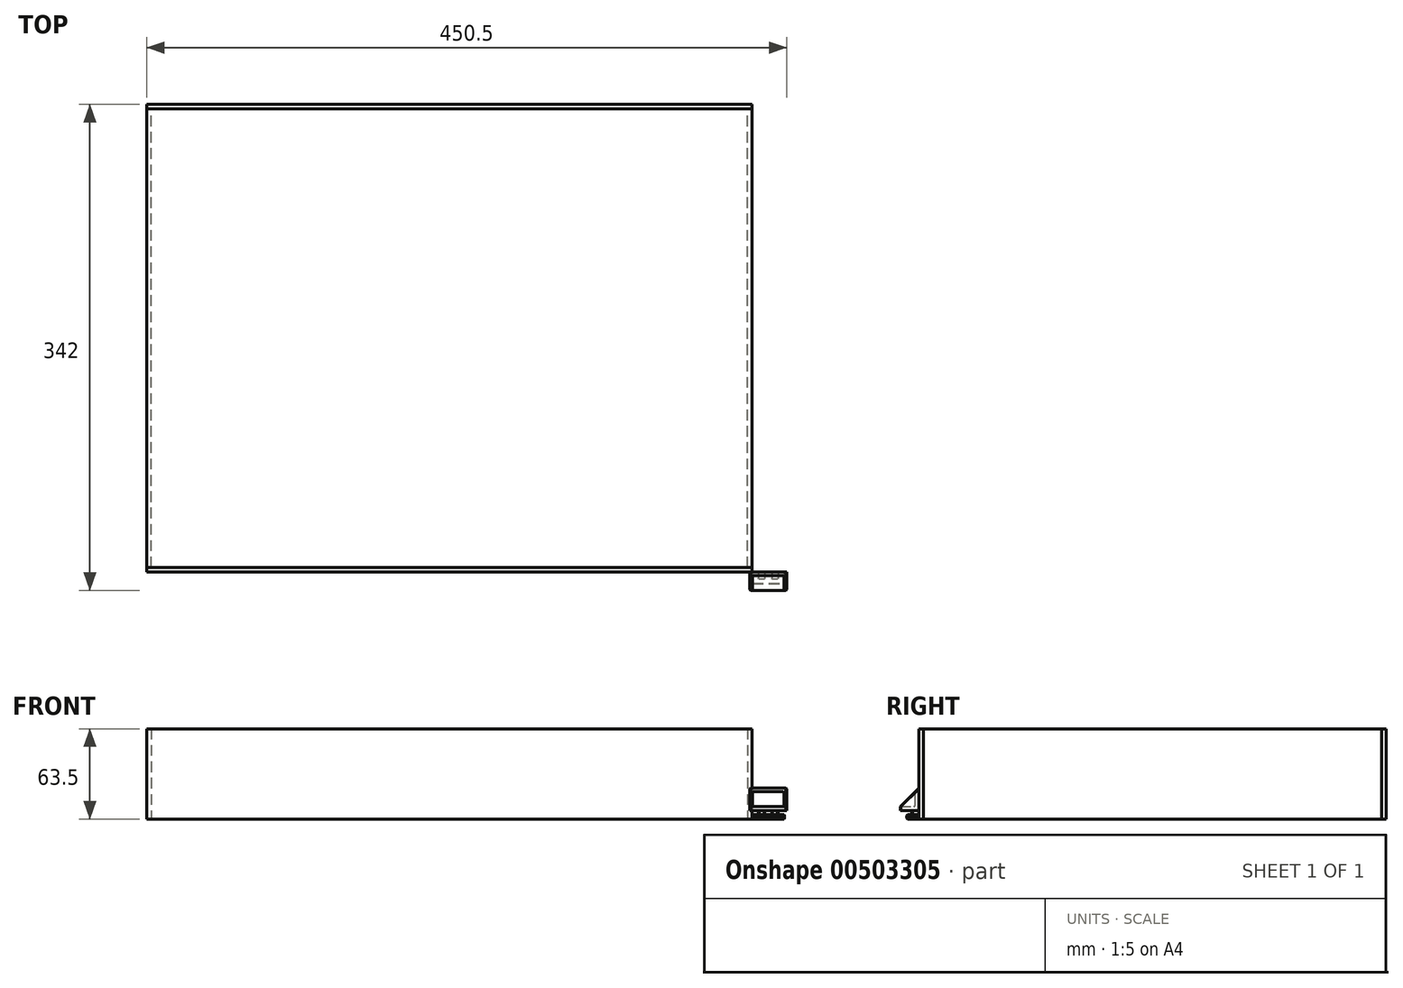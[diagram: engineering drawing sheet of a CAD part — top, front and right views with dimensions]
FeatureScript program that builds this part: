
annotation { "Feature Type Name" : "Feature", "Feature Type Description" : "" }
export const myFeature = defineFeature(function(context is Context, id is Id, definition is map)
    precondition{}
    {
        {
            var Q0;
            Q0=qCreatedBy(makeId("Top.planeOp"),FACE);
            var sketch = newSketch(context, id + "F0", { "sketchPlane" : qUnion([Q0])});
            skLineSegment(sketch, "E0.bottom", {"start": v(0, 0) * mm, "end": v(23, 0) * mm});
            skLineSegment(sketch, "E0.top", {"start": v(0, 8.5) * mm, "end": v(23, 8.5) * mm});
            skLineSegment(sketch, "E0.left", {"start": v(0, 0) * mm, "end": v(0, 8.5) * mm});
            skLineSegment(sketch, "E0.right", {"start": v(23, 0) * mm, "end": v(23, 8.5) * mm});
            skSolve(sketch);
        }
        {
            var Q0;
            Q0=makeQuery(id+"F0.imprint","IMPRINT",FACE,{"disambiguationData":[TD([[makeQuery(id+"F0.imprint","IMPRINT",EDGE,{"derivedFrom":sQuery(id+"F0.wireOp",EDGE,"E0.bottom")}),1.0]])]});
            extrude(context, id + "F1", {"entities" : qUnion([Q0]), "depth" : 3 * mm});
        }
        {
            var Q0;
            Q0=makeQuery(id+"F1.opExtrude","CAP_FACE",FACE,{"disambiguationData":[OSD([sQuery(id+"F0.wireOp",EDGE,"E0.bottom"),sQuery(id+"F0.wireOp",EDGE,"E0.top"),sQuery(id+"F0.wireOp",EDGE,"E0.left"),sQuery(id+"F0.wireOp",EDGE,"E0.right")])],"isStart":false});
            var sketch = newSketch(context, id + "F2", { "sketchPlane" : qUnion([Q0])});
            skLineSegment(sketch, "E1", {"start": v(11.5, 8.5) * mm, "end": v(11.5, 0) * mm, "construction": true});
            skLineSegment(sketch, "E2.bottom", {"start": v(4.57, 8.5) * mm, "end": v(9.07, 8.5) * mm});
            skLineSegment(sketch, "E2.top", {"start": v(4.57, 3.5) * mm, "end": v(9.07, 3.5) * mm});
            skLineSegment(sketch, "E2.left", {"start": v(4.57, 8.5) * mm, "end": v(4.57, 3.5) * mm});
            skLineSegment(sketch, "E2.right", {"start": v(9.07, 8.5) * mm, "end": v(9.07, 3.5) * mm});
            skLineSegment(sketch, "E3.bottom", {"start": v(13.92, 8.5) * mm, "end": v(18.42, 8.5) * mm});
            skLineSegment(sketch, "E3.top", {"start": v(13.92, 3.5) * mm, "end": v(18.42, 3.5) * mm});
            skLineSegment(sketch, "E3.left", {"start": v(13.92, 8.5) * mm, "end": v(13.92, 3.5) * mm});
            skLineSegment(sketch, "E3.right", {"start": v(18.42, 8.5) * mm, "end": v(18.42, 3.5) * mm});
            skSolve(sketch);
        }
        {
            var Q0;
            Q0 = qSketchRegion(id + "F2", true);
            extrude(context, id + "F3", {"entities" : qUnion([Q0]), "operationType" : NewBodyOperationType.ADD, "depth" : 2.85 * mm});
        }
        {
            var Q0;
            Q0=makeQuery(id+"F3.opExtrude","CAP_FACE",FACE,{"disambiguationData":[OSD([sQuery(id+"F2.wireOp",EDGE,"E3.bottom"),sQuery(id+"F2.wireOp",EDGE,"E3.top"),sQuery(id+"F2.wireOp",EDGE,"E3.left"),sQuery(id+"F2.wireOp",EDGE,"E3.right")])],"isStart":false});
            var sketch = newSketch(context, id + "F4", { "sketchPlane" : qUnion([Q0])});
            skLineSegment(sketch, "E4.bottom", {"start": v(24.5, 8.5) * mm, "end": v(-1.5, 8.5) * mm});
            skLineSegment(sketch, "E4.top", {"start": v(24.5, -4.5) * mm, "end": v(-1.5, -4.5) * mm});
            skLineSegment(sketch, "E4.left", {"start": v(24.5, 8.5) * mm, "end": v(24.5, -4.5) * mm});
            skLineSegment(sketch, "E4.right", {"start": v(-1.5, 8.5) * mm, "end": v(-1.5, -4.5) * mm});
            skLineSegment(sketch, "E5", {"start": v(11.5, -4.5) * mm, "end": v(11.5, 8.5) * mm, "construction": true});
            skSolve(sketch);
        }
        {
            var Q0;
            Q0 = qSketchRegion(id + "F4", true);
            extrude(context, id + "F5", {"entities" : qUnion([Q0]), "operationType" : NewBodyOperationType.ADD, "depth" : 3 * mm});
        }
        {
            var Q0;
            Q0=makeQuery(id+"F5.opExtrude","SWEPT_FACE",FACE,{"disambiguationData":[OSD([sQuery(id+"F4.wireOp",EDGE,"E4.left")])]});
            var sketch = newSketch(context, id + "F6", { "sketchPlane" : qUnion([Q0])});
            skLineSegment(sketch, "E6.0", {"start": v(8.5, 8.85) * mm, "end": v(-4.5, 8.85) * mm});
            skLineSegment(sketch, "E7", {"start": v(8.5, 8.85) * mm, "end": v(8.5, 21.85) * mm});
            skLineSegment(sketch, "E8", {"start": v(8.5, 21.85) * mm, "end": v(-4.5, 8.85) * mm});
            skSolve(sketch);
        }
        {
            var Q0;
            Q0=makeQuery(id+"F6.imprint","IMPRINT",FACE,{"disambiguationData":[TD([[makeQuery(id+"F6.imprint","IMPRINT",EDGE,{"derivedFrom":sQuery(id+"F6.wireOp",EDGE,"E6.0")}),-1.0]])]});
            var Q1;
            Q1=makeQuery(id+"F5.opExtrude","SWEPT_FACE",FACE,{"disambiguationData":[OSD([sQuery(id+"F4.wireOp",EDGE,"E4.right")])]});
            extrude(context, id + "F7", {"entities" : qUnion([Q0]), "operationType" : NewBodyOperationType.ADD, "endBound" : BoundingType.UP_TO_SURFACE, "oppositeDirection" : true, "endBoundEntityFace" : qUnion([Q1]), "depth" : 25 * mm});
        }
        {
            var Q0;
            Q0=makeQuery(id+"F3.opExtrude","SWEPT_EDGE",EDGE,{"disambiguationData":[OSD([sQuery(id+"F2.wireOp",EDGE,"E2.top"),sQuery(id+"F2.wireOp",EDGE,"E2.left")])]});
            var Q1;
            Q1=makeQuery(id+"F3.opExtrude","SWEPT_EDGE",EDGE,{"disambiguationData":[OSD([sQuery(id+"F2.wireOp",EDGE,"E2.top"),sQuery(id+"F2.wireOp",EDGE,"E2.right")])]});
            var Q2;
            Q2=makeQuery(id+"F3.opExtrude","SWEPT_EDGE",EDGE,{"disambiguationData":[OSD([sQuery(id+"F2.wireOp",EDGE,"E3.top"),sQuery(id+"F2.wireOp",EDGE,"E3.left")])]});
            var Q3;
            Q3=makeQuery(id+"F3.opExtrude","SWEPT_EDGE",EDGE,{"disambiguationData":[OSD([sQuery(id+"F2.wireOp",EDGE,"E3.top"),sQuery(id+"F2.wireOp",EDGE,"E3.right")])]});
            chamfer(context, id + "F8", {"entities" : qUnion([Q0, Q1, Q2, Q3]), "width" : .5 * mm, "tangentPropagation" : true});
        }
        {
            var Q0;
            Q0=makeQuery(id+"F3.opExtrude","CAP_EDGE",EDGE,{"disambiguationData":[OSD([sQuery(id+"F2.wireOp",EDGE,"E2.left")])],"isStart":false});
            var Q1;
            Q1=makeQuery(id+"F8.opChamfer","BLEND_EDGE",EDGE,{"blendedFrom":[makeQuery(id+"F3.opExtrude","SWEPT_EDGE",EDGE,{"disambiguationData":[OSD([sQuery(id+"F2.wireOp",EDGE,"E2.top"),sQuery(id+"F2.wireOp",EDGE,"E2.left")])]}),makeQuery(id+"F5.opExtrude","CAP_FACE",FACE,{"disambiguationData":[OSD([sQuery(id+"F4.wireOp",EDGE,"E4.bottom"),sQuery(id+"F4.wireOp",EDGE,"E4.top"),sQuery(id+"F4.wireOp",EDGE,"E4.left"),sQuery(id+"F4.wireOp",EDGE,"E4.right")])],"isStart":true})],"blendedInto":[makeQuery(id+"F5.opExtrude","CAP_FACE",FACE,{"disambiguationData":[OSD([sQuery(id+"F4.wireOp",EDGE,"E4.bottom"),sQuery(id+"F4.wireOp",EDGE,"E4.top"),sQuery(id+"F4.wireOp",EDGE,"E4.left"),sQuery(id+"F4.wireOp",EDGE,"E4.right")])],"isStart":true})]});
            var Q2;
            Q2=makeQuery(id+"F3.opExtrude","CAP_EDGE",EDGE,{"disambiguationData":[OSD([sQuery(id+"F2.wireOp",EDGE,"E2.top")])],"isStart":false});
            var Q3;
            Q3=makeQuery(id+"F8.opChamfer","BLEND_EDGE",EDGE,{"blendedFrom":[makeQuery(id+"F3.opExtrude","SWEPT_EDGE",EDGE,{"disambiguationData":[OSD([sQuery(id+"F2.wireOp",EDGE,"E2.top"),sQuery(id+"F2.wireOp",EDGE,"E2.right")])]}),makeQuery(id+"F5.opExtrude","CAP_FACE",FACE,{"disambiguationData":[OSD([sQuery(id+"F4.wireOp",EDGE,"E4.bottom"),sQuery(id+"F4.wireOp",EDGE,"E4.top"),sQuery(id+"F4.wireOp",EDGE,"E4.left"),sQuery(id+"F4.wireOp",EDGE,"E4.right")])],"isStart":true})],"blendedInto":[makeQuery(id+"F5.opExtrude","CAP_FACE",FACE,{"disambiguationData":[OSD([sQuery(id+"F4.wireOp",EDGE,"E4.bottom"),sQuery(id+"F4.wireOp",EDGE,"E4.top"),sQuery(id+"F4.wireOp",EDGE,"E4.left"),sQuery(id+"F4.wireOp",EDGE,"E4.right")])],"isStart":true})]});
            var Q4;
            Q4=makeQuery(id+"F3.opExtrude","CAP_EDGE",EDGE,{"disambiguationData":[OSD([sQuery(id+"F2.wireOp",EDGE,"E2.right")])],"isStart":false});
            var Q5;
            Q5=makeQuery(id+"F3.opExtrude","CAP_EDGE",EDGE,{"disambiguationData":[OSD([sQuery(id+"F2.wireOp",EDGE,"E3.left")])],"isStart":false});
            var Q6;
            Q6=makeQuery(id+"F8.opChamfer","BLEND_EDGE",EDGE,{"blendedFrom":[makeQuery(id+"F3.opExtrude","SWEPT_EDGE",EDGE,{"disambiguationData":[OSD([sQuery(id+"F2.wireOp",EDGE,"E3.top"),sQuery(id+"F2.wireOp",EDGE,"E3.left")])]}),makeQuery(id+"F5.opExtrude","CAP_FACE",FACE,{"disambiguationData":[OSD([sQuery(id+"F4.wireOp",EDGE,"E4.bottom"),sQuery(id+"F4.wireOp",EDGE,"E4.top"),sQuery(id+"F4.wireOp",EDGE,"E4.left"),sQuery(id+"F4.wireOp",EDGE,"E4.right")])],"isStart":true})],"blendedInto":[makeQuery(id+"F5.opExtrude","CAP_FACE",FACE,{"disambiguationData":[OSD([sQuery(id+"F4.wireOp",EDGE,"E4.bottom"),sQuery(id+"F4.wireOp",EDGE,"E4.top"),sQuery(id+"F4.wireOp",EDGE,"E4.left"),sQuery(id+"F4.wireOp",EDGE,"E4.right")])],"isStart":true})]});
            var Q7;
            Q7=makeQuery(id+"F3.opExtrude","CAP_EDGE",EDGE,{"disambiguationData":[OSD([sQuery(id+"F2.wireOp",EDGE,"E3.top")])],"isStart":false});
            var Q8;
            Q8=makeQuery(id+"F8.opChamfer","BLEND_EDGE",EDGE,{"blendedFrom":[makeQuery(id+"F3.opExtrude","SWEPT_EDGE",EDGE,{"disambiguationData":[OSD([sQuery(id+"F2.wireOp",EDGE,"E3.top"),sQuery(id+"F2.wireOp",EDGE,"E3.right")])]}),makeQuery(id+"F5.opExtrude","CAP_FACE",FACE,{"disambiguationData":[OSD([sQuery(id+"F4.wireOp",EDGE,"E4.bottom"),sQuery(id+"F4.wireOp",EDGE,"E4.top"),sQuery(id+"F4.wireOp",EDGE,"E4.left"),sQuery(id+"F4.wireOp",EDGE,"E4.right")])],"isStart":true})],"blendedInto":[makeQuery(id+"F5.opExtrude","CAP_FACE",FACE,{"disambiguationData":[OSD([sQuery(id+"F4.wireOp",EDGE,"E4.bottom"),sQuery(id+"F4.wireOp",EDGE,"E4.top"),sQuery(id+"F4.wireOp",EDGE,"E4.left"),sQuery(id+"F4.wireOp",EDGE,"E4.right")])],"isStart":true})]});
            var Q9;
            Q9=makeQuery(id+"F3.opExtrude","CAP_EDGE",EDGE,{"disambiguationData":[OSD([sQuery(id+"F2.wireOp",EDGE,"E3.right")])],"isStart":false});
            var Q10;
            Q10=makeQuery(id+"F3.opExtrude","CAP_EDGE",EDGE,{"disambiguationData":[OSD([sQuery(id+"F2.wireOp",EDGE,"E3.right")])],"isStart":true});
            var Q11;
            Q11=makeQuery(id+"F8.opChamfer","BLEND_EDGE",EDGE,{"blendedFrom":[makeQuery(id+"F3.opExtrude","SWEPT_EDGE",EDGE,{"disambiguationData":[OSD([sQuery(id+"F2.wireOp",EDGE,"E3.top"),sQuery(id+"F2.wireOp",EDGE,"E3.right")])]}),makeQuery(id+"F1.opExtrude","CAP_FACE",FACE,{"disambiguationData":[OSD([sQuery(id+"F0.wireOp",EDGE,"E0.bottom"),sQuery(id+"F0.wireOp",EDGE,"E0.top"),sQuery(id+"F0.wireOp",EDGE,"E0.left"),sQuery(id+"F0.wireOp",EDGE,"E0.right")])],"isStart":false})],"blendedInto":[makeQuery(id+"F1.opExtrude","CAP_FACE",FACE,{"disambiguationData":[OSD([sQuery(id+"F0.wireOp",EDGE,"E0.bottom"),sQuery(id+"F0.wireOp",EDGE,"E0.top"),sQuery(id+"F0.wireOp",EDGE,"E0.left"),sQuery(id+"F0.wireOp",EDGE,"E0.right")])],"isStart":false})]});
            var Q12;
            Q12=makeQuery(id+"F3.opExtrude","CAP_EDGE",EDGE,{"disambiguationData":[OSD([sQuery(id+"F2.wireOp",EDGE,"E3.top")])],"isStart":true});
            var Q13;
            Q13=makeQuery(id+"F8.opChamfer","BLEND_EDGE",EDGE,{"blendedFrom":[makeQuery(id+"F3.opExtrude","SWEPT_EDGE",EDGE,{"disambiguationData":[OSD([sQuery(id+"F2.wireOp",EDGE,"E3.top"),sQuery(id+"F2.wireOp",EDGE,"E3.left")])]}),makeQuery(id+"F1.opExtrude","CAP_FACE",FACE,{"disambiguationData":[OSD([sQuery(id+"F0.wireOp",EDGE,"E0.bottom"),sQuery(id+"F0.wireOp",EDGE,"E0.top"),sQuery(id+"F0.wireOp",EDGE,"E0.left"),sQuery(id+"F0.wireOp",EDGE,"E0.right")])],"isStart":false})],"blendedInto":[makeQuery(id+"F1.opExtrude","CAP_FACE",FACE,{"disambiguationData":[OSD([sQuery(id+"F0.wireOp",EDGE,"E0.bottom"),sQuery(id+"F0.wireOp",EDGE,"E0.top"),sQuery(id+"F0.wireOp",EDGE,"E0.left"),sQuery(id+"F0.wireOp",EDGE,"E0.right")])],"isStart":false})]});
            var Q14;
            Q14=makeQuery(id+"F3.opExtrude","CAP_EDGE",EDGE,{"disambiguationData":[OSD([sQuery(id+"F2.wireOp",EDGE,"E3.left")])],"isStart":true});
            var Q15;
            Q15=makeQuery(id+"F3.opExtrude","CAP_EDGE",EDGE,{"disambiguationData":[OSD([sQuery(id+"F2.wireOp",EDGE,"E2.top")])],"isStart":true});
            var Q16;
            Q16=makeQuery(id+"F8.opChamfer","BLEND_EDGE",EDGE,{"blendedFrom":[makeQuery(id+"F3.opExtrude","SWEPT_EDGE",EDGE,{"disambiguationData":[OSD([sQuery(id+"F2.wireOp",EDGE,"E2.top"),sQuery(id+"F2.wireOp",EDGE,"E2.left")])]}),makeQuery(id+"F1.opExtrude","CAP_FACE",FACE,{"disambiguationData":[OSD([sQuery(id+"F0.wireOp",EDGE,"E0.bottom"),sQuery(id+"F0.wireOp",EDGE,"E0.top"),sQuery(id+"F0.wireOp",EDGE,"E0.left"),sQuery(id+"F0.wireOp",EDGE,"E0.right")])],"isStart":false})],"blendedInto":[makeQuery(id+"F1.opExtrude","CAP_FACE",FACE,{"disambiguationData":[OSD([sQuery(id+"F0.wireOp",EDGE,"E0.bottom"),sQuery(id+"F0.wireOp",EDGE,"E0.top"),sQuery(id+"F0.wireOp",EDGE,"E0.left"),sQuery(id+"F0.wireOp",EDGE,"E0.right")])],"isStart":false})]});
            var Q17;
            Q17=makeQuery(id+"F3.opExtrude","CAP_EDGE",EDGE,{"disambiguationData":[OSD([sQuery(id+"F2.wireOp",EDGE,"E2.left")])],"isStart":true});
            var Q18;
            Q18=makeQuery(id+"F8.opChamfer","BLEND_EDGE",EDGE,{"blendedFrom":[makeQuery(id+"F3.opExtrude","SWEPT_EDGE",EDGE,{"disambiguationData":[OSD([sQuery(id+"F2.wireOp",EDGE,"E2.top"),sQuery(id+"F2.wireOp",EDGE,"E2.right")])]}),makeQuery(id+"F1.opExtrude","CAP_FACE",FACE,{"disambiguationData":[OSD([sQuery(id+"F0.wireOp",EDGE,"E0.bottom"),sQuery(id+"F0.wireOp",EDGE,"E0.top"),sQuery(id+"F0.wireOp",EDGE,"E0.left"),sQuery(id+"F0.wireOp",EDGE,"E0.right")])],"isStart":false})],"blendedInto":[makeQuery(id+"F1.opExtrude","CAP_FACE",FACE,{"disambiguationData":[OSD([sQuery(id+"F0.wireOp",EDGE,"E0.bottom"),sQuery(id+"F0.wireOp",EDGE,"E0.top"),sQuery(id+"F0.wireOp",EDGE,"E0.left"),sQuery(id+"F0.wireOp",EDGE,"E0.right")])],"isStart":false})]});
            var Q19;
            Q19=makeQuery(id+"F3.opExtrude","CAP_EDGE",EDGE,{"disambiguationData":[OSD([sQuery(id+"F2.wireOp",EDGE,"E2.right")])],"isStart":true});
            fillet(context, id + "F9", {"entities" : qUnion([Q0, Q1, Q2, Q3, Q4, Q5, Q6, Q7, Q8, Q9, Q10, Q11, Q12, Q13, Q14, Q15, Q16, Q17, Q18, Q19]), "radius" : .25 * mm, "tangentPropagation" : true, "allowEdgeOverflow" : false});
        }
        {
            var Q0;
            Q0=makeQuery(id+"F1.opExtrude","CAP_EDGE",EDGE,{"disambiguationData":[OSD([sQuery(id+"F0.wireOp",EDGE,"E0.left")])],"isStart":false});
            var Q1;
            Q1=makeQuery(id+"F1.opExtrude","SWEPT_EDGE",EDGE,{"disambiguationData":[OSD([sQuery(id+"F0.wireOp",EDGE,"E0.bottom"),sQuery(id+"F0.wireOp",EDGE,"E0.left")])]});
            var Q2;
            Q2=makeQuery(id+"F1.opExtrude","CAP_EDGE",EDGE,{"disambiguationData":[OSD([sQuery(id+"F0.wireOp",EDGE,"E0.left")])],"isStart":true});
            var Q3;
            Q3=makeQuery(id+"F1.opExtrude","CAP_EDGE",EDGE,{"disambiguationData":[OSD([sQuery(id+"F0.wireOp",EDGE,"E0.bottom")])],"isStart":false});
            var Q4;
            Q4=makeQuery(id+"F1.opExtrude","CAP_EDGE",EDGE,{"disambiguationData":[OSD([sQuery(id+"F0.wireOp",EDGE,"E0.bottom")])],"isStart":true});
            var Q5;
            Q5=makeQuery(id+"F1.opExtrude","CAP_EDGE",EDGE,{"disambiguationData":[OSD([sQuery(id+"F0.wireOp",EDGE,"E0.right")])],"isStart":false});
            var Q6;
            Q6=makeQuery(id+"F1.opExtrude","SWEPT_EDGE",EDGE,{"disambiguationData":[OSD([sQuery(id+"F0.wireOp",EDGE,"E0.bottom"),sQuery(id+"F0.wireOp",EDGE,"E0.right")])]});
            var Q7;
            Q7=makeQuery(id+"F1.opExtrude","CAP_EDGE",EDGE,{"disambiguationData":[OSD([sQuery(id+"F0.wireOp",EDGE,"E0.right")])],"isStart":true});
            chamfer(context, id + "F10", {"entities" : qUnion([Q0, Q1, Q2, Q3, Q4, Q5, Q6, Q7]), "width" : .5 * mm, "tangentPropagation" : true});
        }
        {
            var Q0;
            Q0=qCreatedBy(makeId("Top.planeOp"),FACE);
            var sketch = newSketch(context, id + "F11", { "sketchPlane" : qUnion([Q0])});
            skLineSegment(sketch, "E9.bottom", {"start": v(0, 8.5) * mm, "end": v(-426, 8.5) * mm});
            skLineSegment(sketch, "E9.top", {"start": v(0, 337.5) * mm, "end": v(-426, 337.5) * mm});
            skLineSegment(sketch, "E9.left", {"start": v(0, 8.5) * mm, "end": v(0, 337.5) * mm});
            skLineSegment(sketch, "E9.right", {"start": v(-426, 8.5) * mm, "end": v(-426, 337.5) * mm});
            skLineSegment(sketch, "E10", {"start": v(-426, 334.32) * mm, "end": v(0, 334.33) * mm});
            skLineSegment(sketch, "E11", {"start": v(-426, 11.67) * mm, "end": v(0, 11.67) * mm});
            skLineSegment(sketch, "E12", {"start": v(-422.82, 11.67) * mm, "end": v(-422.83, 334.32) * mm});
            skLineSegment(sketch, "E13", {"start": v(-3.17, 11.67) * mm, "end": v(-3.18, 334.33) * mm});
            skLineSegment(sketch, "E14", {"start": v(-426, 173) * mm, "end": v(-422.82, 173) * mm, "construction": true});
            skPoint(sketch, "E14.startSnap0", {"position": v(-422.82, 173) * mm});
            skLineSegment(sketch, "E15", {"start": v(-213, 334.33) * mm, "end": v(-213, 337.5) * mm, "construction": true});
            skSolve(sketch);
        }
        {
            var Q0;
            {var subQ4=sQuery(id+"F11.wireOp",EDGE,"E9.bottom");Q0=makeQuery(id+"F11.imprint","IMPRINT",FACE,{"disambiguationData":[TD([[makeQuery(id+"F11.imprint","IMPRINT",EDGE,{"derivedFrom":subQ4}),-1.0]])]});}
            var Q1;
            {var subQ4=sQuery(id+"F11.wireOp",EDGE,"E9.top");Q1=makeQuery(id+"F11.imprint","IMPRINT",FACE,{"disambiguationData":[TD([[makeQuery(id+"F11.imprint","IMPRINT",EDGE,{"derivedFrom":subQ4}),1.0]])]});}
            extrude(context, id + "F12", {"entities" : qUnion([Q0, Q1]), "depth" : 63.5 * mm});
        }
        {
            var Q0;
            {var subQ5=sQuery(id+"F11.wireOp",EDGE,"E13");Q0=makeQuery(id+"F11.imprint","IMPRINT",FACE,{"disambiguationData":[TD([[makeQuery(id+"F11.imprint","IMPRINT",EDGE,{"derivedFrom":subQ5}),-1.0]])]});}
            var Q1;
            {var subQ5=sQuery(id+"F11.wireOp",EDGE,"E12");Q1=makeQuery(id+"F11.imprint","IMPRINT",FACE,{"disambiguationData":[TD([[makeQuery(id+"F11.imprint","IMPRINT",EDGE,{"derivedFrom":subQ5}),1.0]])]});}
            var Q2;
            Q2=makeQuery(id+"F12.opExtrude","CAP_FACE",FACE,{"disambiguationData":[OSD([sQuery(id+"F11.wireOp",EDGE,"E9.bottom"),sQuery(id+"F11.wireOp",EDGE,"E9.left"),sQuery(id+"F11.wireOp",EDGE,"E9.right"),sQuery(id+"F11.wireOp",EDGE,"E11")])],"isStart":false});
            extrude(context, id + "F13", {"entities" : qUnion([Q0, Q1]), "endBound" : BoundingType.UP_TO_SURFACE, "endBoundEntityFace" : qUnion([Q2]), "depth" : 25 * mm});
        }
        {
            var Q0;
            Q0=makeQuery(id+"F12.opExtrude","CAP_FACE",FACE,{"disambiguationData":[OSD([sQuery(id+"F11.wireOp",EDGE,"E9.bottom"),sQuery(id+"F11.wireOp",EDGE,"E9.left"),sQuery(id+"F11.wireOp",EDGE,"E9.right"),sQuery(id+"F11.wireOp",EDGE,"E11")])],"isStart":false});
            var sketch = newSketch(context, id + "F14", { "sketchPlane" : qUnion([Q0])});
            skLineSegment(sketch, "E16.0", {"start": v(0, 8.5) * mm, "end": v(-426, 8.5) * mm});
            skLineSegment(sketch, "E16.1", {"start": v(-426, 8.5) * mm, "end": v(-426, 337.5) * mm});
            skLineSegment(sketch, "E16.2", {"start": v(0, 337.5) * mm, "end": v(-426, 337.5) * mm});
            skLineSegment(sketch, "E16.3", {"start": v(0, 8.5) * mm, "end": v(0, 337.5) * mm});
            skSolve(sketch);
        }
        {
            var Q0;
            Q0 = qSketchRegion(id + "F14", true);
            extrude(context, id + "F15", {"entities" : qUnion([Q0]), "depth" : 1 / 203.2 * mm});
        }
        {
            var Q0;
            Q0=makeQuery(id+"F7.boolean.opBoolean","MERGE",FACE,{"derivedFrom":[makeQuery(id+"F5.opExtrude","SWEPT_FACE",FACE,{"disambiguationData":[OSD([sQuery(id+"F4.wireOp",EDGE,"E4.left")])]}),makeQuery(id+"F7.opExtrude","CAP_FACE",FACE,{"disambiguationData":[OSD([sQuery(id+"F6.wireOp",EDGE,"E6.0"),sQuery(id+"F6.wireOp",EDGE,"E7"),sQuery(id+"F6.wireOp",EDGE,"E8")])],"isStart":true})]});
            var sketch = newSketch(context, id + "F16", { "sketchPlane" : qUnion([Q0])});
            skLineSegment(sketch, "E17", {"start": v(-4.5, 8.85) * mm, "end": v(6, 8.85) * mm});
            skLineSegment(sketch, "E18", {"start": v(6, 8.85) * mm, "end": v(6, 19.35) * mm});
            skLineSegment(sketch, "E19.0", {"start": v(8.5, 21.85) * mm, "end": v(-4.5, 8.85) * mm});
            skSolve(sketch);
        }
        {
            var Q0;
            {var subQ0=sQuery(id+"F16.wireOp",EDGE,"E17");Q0=makeQuery(id+"F16.imprint","IMPRINT",FACE,{"disambiguationData":[TD([[makeQuery(id+"F16.imprint","IMPRINT",EDGE,{"derivedFrom":subQ0}),1.0]])]});}
            extrude(context, id + "F17", {"entities" : qUnion([Q0]), "operationType" : NewBodyOperationType.REMOVE, "oppositeDirection" : true, "depth" : 24 * mm, "hasSecondDirection" : true, "secondDirectionOppositeDirection" : true, "secondDirectionDepth" : 2 * mm});
        }
        {
            var Q0;
            Q0=makeQuery(id+"F7.opExtrude","CAP_EDGE",EDGE,{"disambiguationData":[OSD([sQuery(id+"F6.wireOp",EDGE,"E8")])],"isStart":true});
            var Q1;
            Q1=makeQuery(id+"F5.opExtrude","SWEPT_EDGE",EDGE,{"disambiguationData":[OSD([sQuery(id+"F4.wireOp",EDGE,"E4.top"),sQuery(id+"F4.wireOp",EDGE,"E4.left")])]});
            var Q2;
            Q2=makeQuery(id+"F5.opExtrude","SWEPT_EDGE",EDGE,{"disambiguationData":[OSD([sQuery(id+"F4.wireOp",EDGE,"E4.top"),sQuery(id+"F4.wireOp",EDGE,"E4.right")])]});
            var Q3;
            Q3=makeQuery(id+"F7.opExtrude","CAP_EDGE",EDGE,{"disambiguationData":[OSD([sQuery(id+"F6.wireOp",EDGE,"E8")])],"isStart":false});
            chamfer(context, id + "F18", {"entities" : qUnion([Q0, Q1, Q2, Q3]), "width" : .5 * mm, "tangentPropagation" : true});
        }
        {
            var Q0;
            Q0=makeQuery(id+"F17.boolean.opBoolean","COPY",EDGE,{"derivedFrom":makeQuery(id+"F17.opExtrude","SWEPT_EDGE",EDGE,{"disambiguationData":[OSD([sQuery(id+"F16.wireOp",EDGE,"E17"),sQuery(id+"F16.wireOp",EDGE,"E18")])]})});
            var Q1;
            Q1=makeQuery(id+"F17.boolean.opBoolean","COPY",EDGE,{"derivedFrom":makeQuery(id+"F17.opExtrude","CAP_EDGE",EDGE,{"disambiguationData":[OSD([sQuery(id+"F16.wireOp",EDGE,"E18")])],"isStart":false})});
            var Q2;
            Q2=makeQuery(id+"F17.boolean.opBoolean","COPY",EDGE,{"derivedFrom":makeQuery(id+"F17.opExtrude","CAP_EDGE",EDGE,{"disambiguationData":[OSD([sQuery(id+"F16.wireOp",EDGE,"E17")])],"isStart":false})});
            var Q3;
            Q3=makeQuery(id+"F17.boolean.opBoolean","COPY",EDGE,{"derivedFrom":makeQuery(id+"F17.opExtrude","CAP_EDGE",EDGE,{"disambiguationData":[OSD([sQuery(id+"F16.wireOp",EDGE,"E18")])],"isStart":true})});
            var Q4;
            Q4=makeQuery(id+"F17.boolean.opBoolean","COPY",EDGE,{"derivedFrom":makeQuery(id+"F17.opExtrude","CAP_EDGE",EDGE,{"disambiguationData":[OSD([sQuery(id+"F16.wireOp",EDGE,"E17")])],"isStart":true})});
            fillet(context, id + "F19", {"entities" : qUnion([Q0, Q1, Q2, Q3, Q4]), "radius" : 1 * mm, "tangentPropagation" : true, "allowEdgeOverflow" : false});
        }
    });
